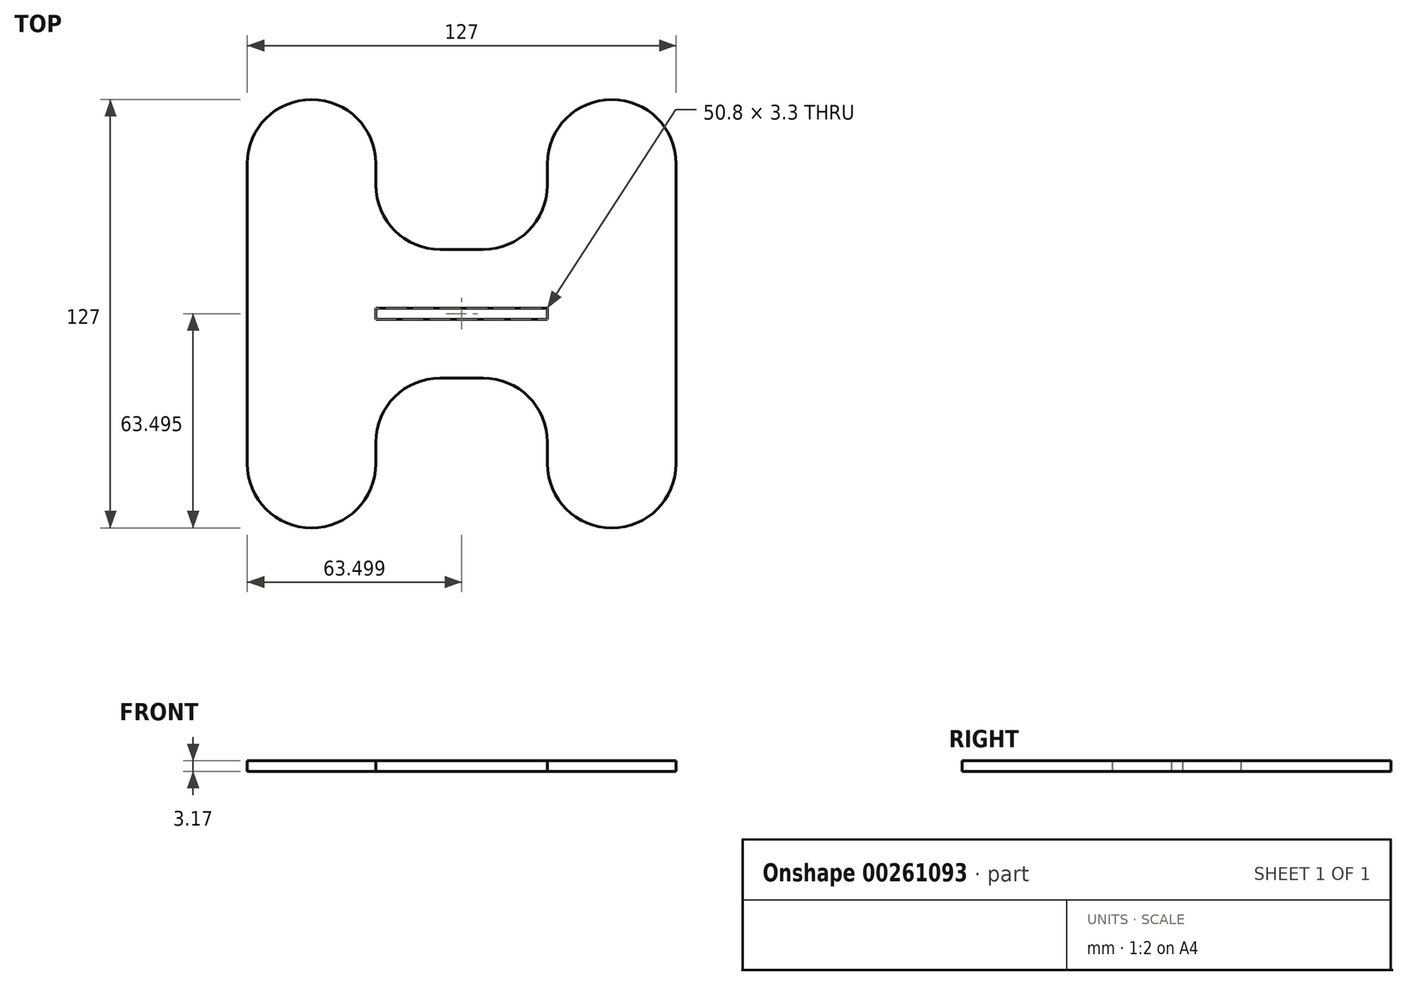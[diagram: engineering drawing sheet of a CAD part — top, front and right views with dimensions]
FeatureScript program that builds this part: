
annotation { "Feature Type Name" : "Feature", "Feature Type Description" : "" }
export const myFeature = defineFeature(function(context is Context, id is Id, definition is map)
    precondition{}
    {
        {
            var Q0;
            Q0=qCreatedBy(makeId("Top.planeOp"),FACE);
            var sketch = newSketch(context, id + "F0", { "sketchPlane" : qUnion([Q0])});
            skLineSegment(sketch, "E0.bottom", {"start": v(-19.33, 68.64) * mm, "end": v(18.77, 68.64) * mm});
            skLineSegment(sketch, "E0.top", {"start": v(-19.33, -58.36) * mm, "end": v(18.77, -58.36) * mm});
            skLineSegment(sketch, "E0.left", {"start": v(-19.33, 68.64) * mm, "end": v(-19.33, -58.36) * mm});
            skLineSegment(sketch, "E1.bottom", {"start": v(18.77, 24.19) * mm, "end": v(69.57, 24.19) * mm});
            skLineSegment(sketch, "E1.top", {"start": v(18.77, -13.91) * mm, "end": v(69.57, -13.91) * mm});
            skLineSegment(sketch, "E2.bottom", {"start": v(69.57, 68.64) * mm, "end": v(107.67, 68.64) * mm});
            skLineSegment(sketch, "E2.top", {"start": v(69.57, -58.36) * mm, "end": v(107.67, -58.36) * mm});
            skLineSegment(sketch, "E2.right", {"start": v(107.67, 68.64) * mm, "end": v(107.67, -58.36) * mm});
            skLineSegment(sketch, "E3", {"start": v(18.77, 24.19) * mm, "end": v(18.77, 68.64) * mm});
            skLineSegment(sketch, "E4", {"start": v(18.77, -13.91) * mm, "end": v(18.77, -58.36) * mm});
            skLineSegment(sketch, "E5", {"start": v(69.57, 24.19) * mm, "end": v(69.57, 68.64) * mm});
            skLineSegment(sketch, "E6", {"start": v(69.57, -13.91) * mm, "end": v(69.57, -58.36) * mm});
            skLineSegment(sketch, "E7.bottom", {"start": v(18.77, 6.79) * mm, "end": v(69.57, 6.79) * mm});
            skLineSegment(sketch, "E7.top", {"start": v(18.77, 3.48) * mm, "end": v(69.57, 3.48) * mm});
            skLineSegment(sketch, "E7.left", {"start": v(18.77, 6.79) * mm, "end": v(18.77, 3.48) * mm});
            skLineSegment(sketch, "E7.right", {"start": v(69.57, 6.79) * mm, "end": v(69.57, 3.48) * mm});
            skLineSegment(sketch, "E8", {"start": v(18.77, 6.79) * mm, "end": v(18.77, 24.19) * mm, "construction": true});
            skLineSegment(sketch, "E9", {"start": v(18.77, -13.91) * mm, "end": v(18.77, 3.48) * mm, "construction": true});
            skSolve(sketch);
        }
        {
            var Q0;
            Q0=makeQuery(id+"F0.imprint","IMPRINT",FACE,{"disambiguationData":[TD([[makeQuery(id+"F0.imprint","IMPRINT",EDGE,{"derivedFrom":sQuery(id+"F0.wireOp",EDGE,"E0.bottom")}),-1.0]])]});
            extrude(context, id + "F1", {"entities" : qUnion([Q0]), "depth" : 3.17 * mm});
        }
        {
            var Q0;
            Q0=makeQuery(id+"F1.opExtrude","SWEPT_EDGE",EDGE,{"disambiguationData":[OSD([sQuery(id+"F0.wireOp",EDGE,"E0.top"),sQuery(id+"F0.wireOp",EDGE,"E4")])]});
            var Q1;
            Q1=makeQuery(id+"F1.opExtrude","SWEPT_EDGE",EDGE,{"disambiguationData":[OSD([sQuery(id+"F0.wireOp",EDGE,"E0.top"),sQuery(id+"F0.wireOp",EDGE,"E0.left")])]});
            var Q2;
            Q2=makeQuery(id+"F1.opExtrude","SWEPT_EDGE",EDGE,{"disambiguationData":[OSD([sQuery(id+"F0.wireOp",EDGE,"E2.top"),sQuery(id+"F0.wireOp",EDGE,"E6")])]});
            var Q3;
            Q3=makeQuery(id+"F1.opExtrude","SWEPT_EDGE",EDGE,{"disambiguationData":[OSD([sQuery(id+"F0.wireOp",EDGE,"E2.top"),sQuery(id+"F0.wireOp",EDGE,"E2.right")])]});
            var Q4;
            Q4=makeQuery(id+"F1.opExtrude","SWEPT_EDGE",EDGE,{"disambiguationData":[OSD([sQuery(id+"F0.wireOp",EDGE,"E1.top"),sQuery(id+"F0.wireOp",EDGE,"E4")])]});
            var Q5;
            Q5=makeQuery(id+"F1.opExtrude","SWEPT_EDGE",EDGE,{"disambiguationData":[OSD([sQuery(id+"F0.wireOp",EDGE,"E1.top"),sQuery(id+"F0.wireOp",EDGE,"E6")])]});
            var Q6;
            Q6=makeQuery(id+"F1.opExtrude","SWEPT_EDGE",EDGE,{"disambiguationData":[OSD([sQuery(id+"F0.wireOp",EDGE,"E0.bottom"),sQuery(id+"F0.wireOp",EDGE,"E0.left")])]});
            var Q7;
            Q7=makeQuery(id+"F1.opExtrude","SWEPT_EDGE",EDGE,{"disambiguationData":[OSD([sQuery(id+"F0.wireOp",EDGE,"E0.bottom"),sQuery(id+"F0.wireOp",EDGE,"E3")])]});
            var Q8;
            Q8=makeQuery(id+"F1.opExtrude","SWEPT_EDGE",EDGE,{"disambiguationData":[OSD([sQuery(id+"F0.wireOp",EDGE,"E1.bottom"),sQuery(id+"F0.wireOp",EDGE,"E5")])]});
            var Q9;
            Q9=makeQuery(id+"F1.opExtrude","SWEPT_EDGE",EDGE,{"disambiguationData":[OSD([sQuery(id+"F0.wireOp",EDGE,"E2.bottom"),sQuery(id+"F0.wireOp",EDGE,"E5")])]});
            var Q10;
            Q10=makeQuery(id+"F1.opExtrude","SWEPT_EDGE",EDGE,{"disambiguationData":[OSD([sQuery(id+"F0.wireOp",EDGE,"E2.bottom"),sQuery(id+"F0.wireOp",EDGE,"E2.right")])]});
            var Q11;
            Q11=makeQuery(id+"F1.opExtrude","SWEPT_EDGE",EDGE,{"disambiguationData":[OSD([sQuery(id+"F0.wireOp",EDGE,"E1.bottom"),sQuery(id+"F0.wireOp",EDGE,"E3")])]});
            fillet(context, id + "F2", {"entities" : qUnion([Q0, Q1, Q2, Q3, Q4, Q5, Q6, Q7, Q8, Q9, Q10, Q11]), "radius" : 19.05 * mm, "tangentPropagation" : true, "allowEdgeOverflow" : false});
        }
    });
